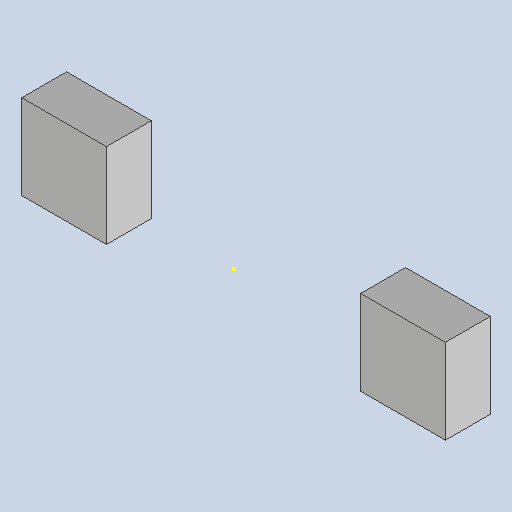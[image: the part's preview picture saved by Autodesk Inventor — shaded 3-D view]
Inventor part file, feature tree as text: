
AUTODESK INVENTOR PART (.ipt)
format: ipt  version: 2024.2 (Build 282272000, 272)  size: 88,576 bytes
history: native  units: mm
features: sketch x2, extrude x1
ambient origin geometry x8: Origin, YZ Plane, XZ Plane, XY Plane, X Axis, Y Axis, Z Axis, Center Point
bodies: Solid1 (feature_tree)
feature tree (3):
  sketch  "Sketch1"  dims[d0=17.0mm d1=17.0mm]
  extrude  "Extrusion1"  Depth=17.0mm
  sketch  "Sketch2"  dims[d2=17.0mm d3=17.0mm d4=51.0mm d5=9.0mm d6=0.0mm]
